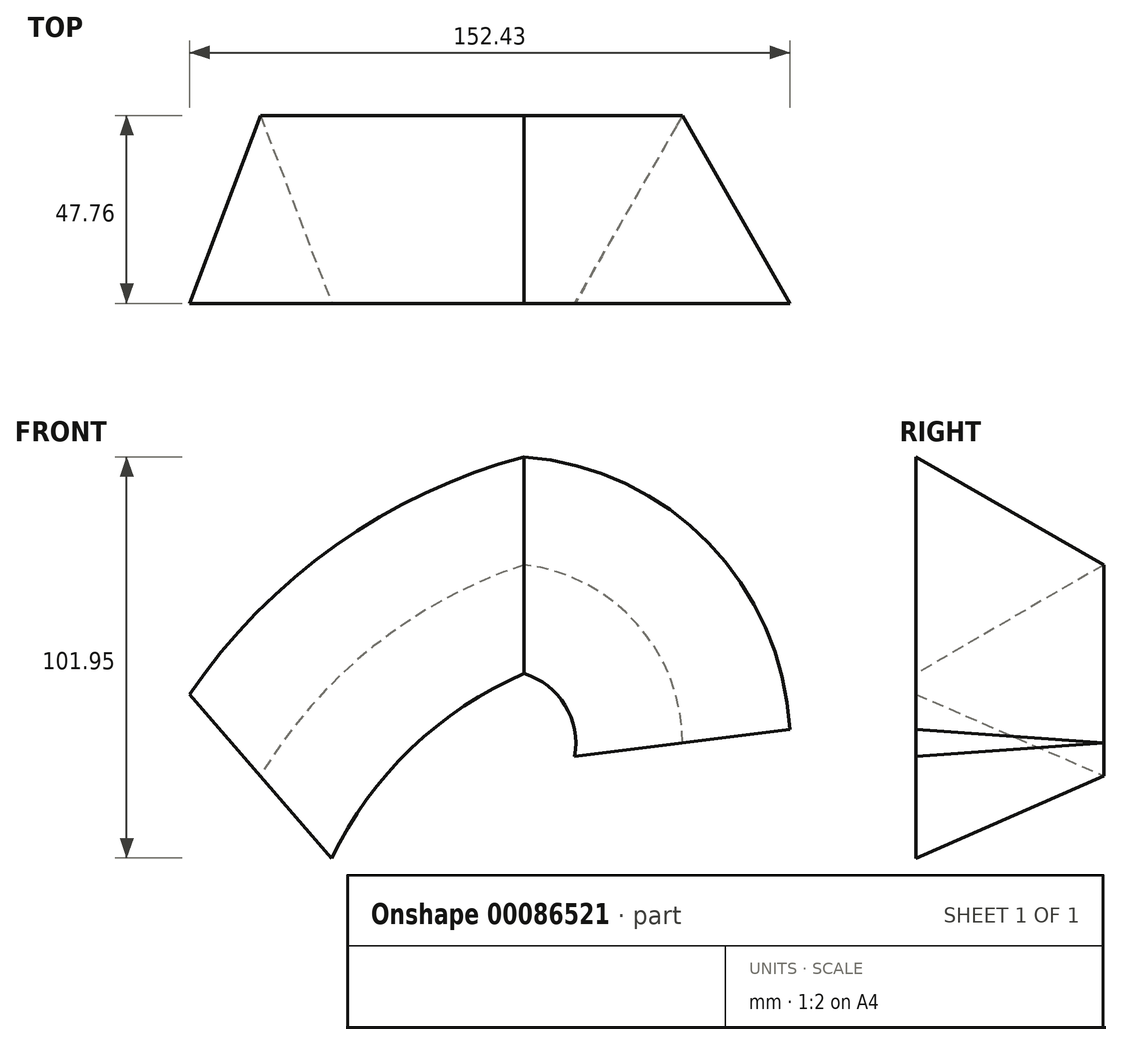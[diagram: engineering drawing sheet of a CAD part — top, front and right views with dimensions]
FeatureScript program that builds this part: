
annotation { "Feature Type Name" : "Feature", "Feature Type Description" : "" }
export const myFeature = defineFeature(function(context is Context, id is Id, definition is map)
    precondition{}
    {
        {
            var Q0;
            Q0=qCreatedBy(makeId("Front.planeOp"),FACE);
            var sketch = newSketch(context, id + "F0", { "sketchPlane" : qUnion([Q0])});
            skArc(sketch, "E0", {"start": v(40.18, -24.2) * mm, "mid": v(28.63, 5.98) * mm, "end": v(0, 20.97) * mm});
            skSolve(sketch);
        }
        {
            var Q0;
            Q0=qCreatedBy(makeId("Right.planeOp"),FACE);
            var sketch = newSketch(context, id + "F1", { "sketchPlane" : qUnion([Q0])});
            skCircle(sketch, "E1.cCircle", {"center": v(0, 20.97) * mm, "radius": 15.9 * mm, "construction": true});
            skLineSegment(sketch, "E1.0", {"start": v(-15.96, 48.47) * mm, "end": v(31.8, 21.04) * mm});
            skLineSegment(sketch, "E1.1", {"start": v(31.8, 21.04) * mm, "end": v(-15.84, -6.6) * mm});
            skLineSegment(sketch, "E1.2", {"start": v(-15.84, -6.6) * mm, "end": v(-15.96, 48.47) * mm});
            skPoint(sketch, "E1.0.midPoint", {"position": v(7.92, 34.76) * mm});
            skSolve(sketch);
        }
        {
            var Q0;
            Q0=makeQuery(id+"F1.imprint","IMPRINT",FACE,{"disambiguationData":[TD([[makeQuery(id+"F1.imprint","IMPRINT",EDGE,{"derivedFrom":sQuery(id+"F1.wireOp",EDGE,"E1.0")}),-1.0]])]});
            var Q1;
            Q1=sQuery(id+"F0.wireOp",EDGE,"E0");
            sweep(context, id + "F2", {"profiles" : qUnion([Q0]), "path" : qUnion([Q1])});
        }
        {
            var Q0;
            Q0=qCreatedBy(makeId("Front.planeOp"),FACE);
            var sketch = newSketch(context, id + "F3", { "sketchPlane" : qUnion([Q0])});
            skArc(sketch, "E2", {"start": v(0, 21.26) * mm, "mid": v(-38.42, 0.48) * mm, "end": v(-67.16, -32.4) * mm});
            skSolve(sketch);
        }
        {
            var Q0;
            Q0 = qSketchRegion(id + "F1", true);
            var Q1;
            Q1=sQuery(id+"F3.wireOp",EDGE,"E2");
            sweep(context, id + "F4", {"operationType" : NewBodyOperationType.ADD, "profiles" : qUnion([Q0]), "path" : qUnion([Q1])});
        }
    });
